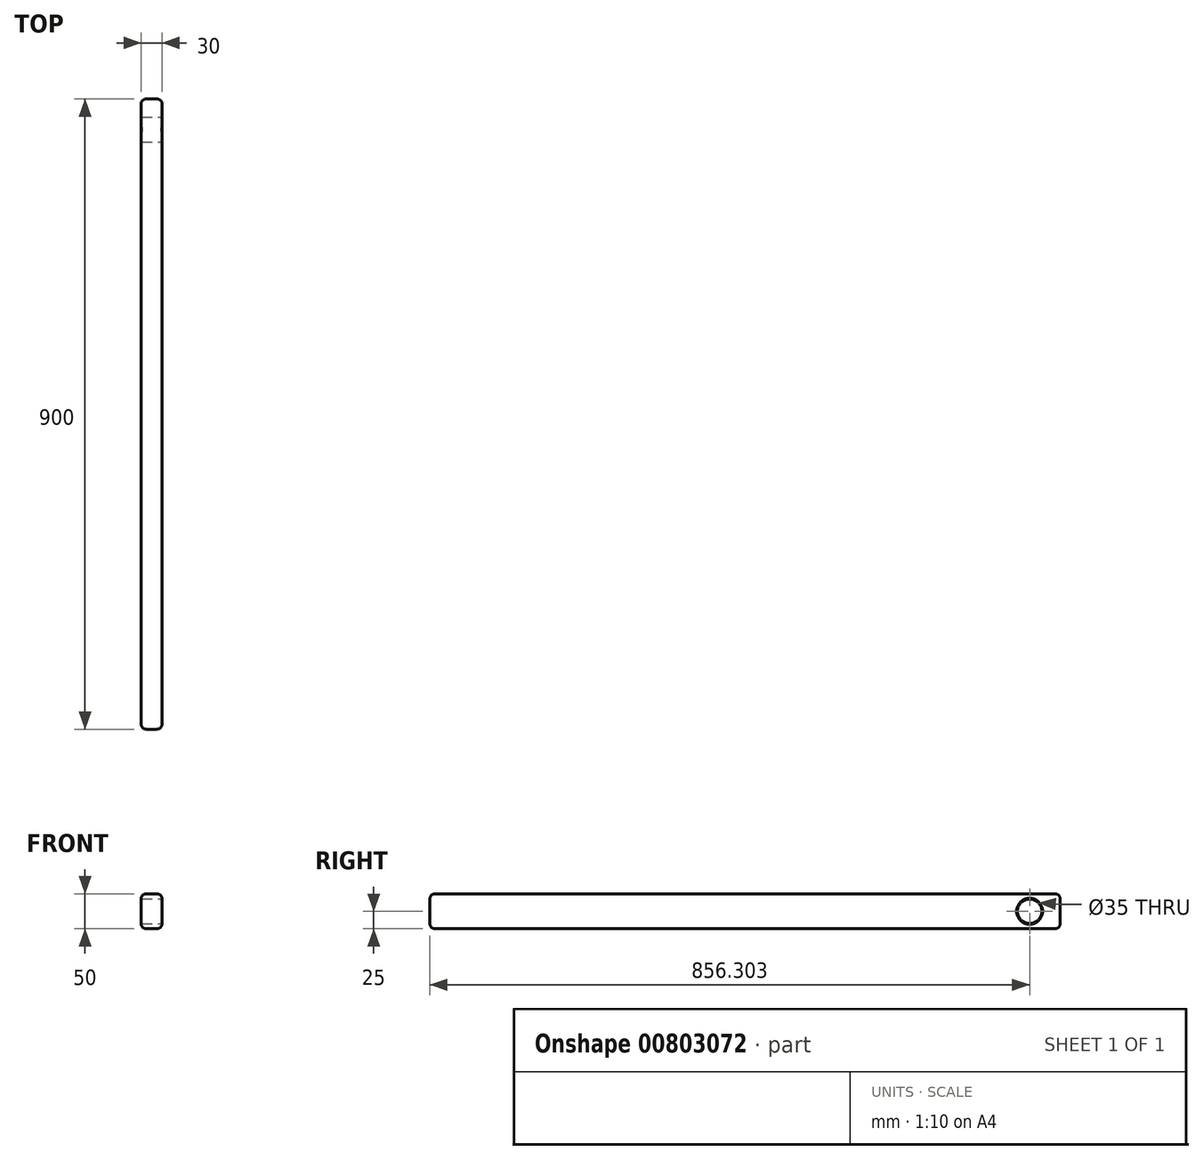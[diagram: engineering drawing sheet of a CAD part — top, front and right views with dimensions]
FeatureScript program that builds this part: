
annotation { "Feature Type Name" : "Feature", "Feature Type Description" : "" }
export const myFeature = defineFeature(function(context is Context, id is Id, definition is map)
    precondition{}
    {
        {
            var Q0;
            Q0=qCreatedBy(makeId("Front.planeOp"),FACE);
            var sketch = newSketch(context, id + "F0", { "sketchPlane" : qUnion([Q0])});
            skLineSegment(sketch, "E0.bottom", {"start": v(0, 0) * mm, "end": v(30, 0) * mm});
            skLineSegment(sketch, "E0.top", {"start": v(0, -50) * mm, "end": v(30, -50) * mm});
            skLineSegment(sketch, "E0.left", {"start": v(0, 0) * mm, "end": v(0, -50) * mm});
            skLineSegment(sketch, "E0.right", {"start": v(30, 0) * mm, "end": v(30, -50) * mm});
            skSolve(sketch);
        }
        {
            var Q0;
            Q0=makeQuery(id+"F0.imprint","IMPRINT",FACE,{"disambiguationData":[TD([[makeQuery(id+"F0.imprint","IMPRINT",EDGE,{"derivedFrom":sQuery(id+"F0.wireOp",EDGE,"E0.bottom")}),-1.0]])]});
            extrude(context, id + "F1", {"entities" : qUnion([Q0]), "depth" : 900 * mm, "offsetDistance" : 25.4 * mm});
        }
        {
            var Q0;
            Q0=makeQuery(id+"F1.opExtrude","SWEPT_EDGE",EDGE,{"disambiguationData":[OSD([sQuery(id+"F0.wireOp",EDGE,"E0.bottom"),sQuery(id+"F0.wireOp",EDGE,"E0.left")])]});
            var Q1;
            Q1=makeQuery(id+"F1.opExtrude","SWEPT_EDGE",EDGE,{"disambiguationData":[OSD([sQuery(id+"F0.wireOp",EDGE,"E0.bottom"),sQuery(id+"F0.wireOp",EDGE,"E0.right")])]});
            var Q2;
            Q2=makeQuery(id+"F1.opExtrude","CAP_EDGE",EDGE,{"disambiguationData":[OSD([sQuery(id+"F0.wireOp",EDGE,"E0.bottom")])],"isStart":true});
            var Q3;
            Q3=makeQuery(id+"F1.opExtrude","CAP_EDGE",EDGE,{"disambiguationData":[OSD([sQuery(id+"F0.wireOp",EDGE,"E0.left")])],"isStart":true});
            var Q4;
            Q4=makeQuery(id+"F1.opExtrude","CAP_EDGE",EDGE,{"disambiguationData":[OSD([sQuery(id+"F0.wireOp",EDGE,"E0.top")])],"isStart":true});
            var Q5;
            Q5=makeQuery(id+"F1.opExtrude","CAP_EDGE",EDGE,{"disambiguationData":[OSD([sQuery(id+"F0.wireOp",EDGE,"E0.right")])],"isStart":true});
            var Q6;
            Q6=makeQuery(id+"F1.opExtrude","SWEPT_EDGE",EDGE,{"disambiguationData":[OSD([sQuery(id+"F0.wireOp",EDGE,"E0.top"),sQuery(id+"F0.wireOp",EDGE,"E0.right")])]});
            var Q7;
            Q7=makeQuery(id+"F1.opExtrude","SWEPT_EDGE",EDGE,{"disambiguationData":[OSD([sQuery(id+"F0.wireOp",EDGE,"E0.top"),sQuery(id+"F0.wireOp",EDGE,"E0.left")])]});
            var Q8;
            Q8=makeQuery(id+"F1.opExtrude","CAP_EDGE",EDGE,{"disambiguationData":[OSD([sQuery(id+"F0.wireOp",EDGE,"E0.top")])],"isStart":false});
            var Q9;
            Q9=makeQuery(id+"F1.opExtrude","CAP_EDGE",EDGE,{"disambiguationData":[OSD([sQuery(id+"F0.wireOp",EDGE,"E0.left")])],"isStart":false});
            var Q10;
            Q10=makeQuery(id+"F1.opExtrude","CAP_EDGE",EDGE,{"disambiguationData":[OSD([sQuery(id+"F0.wireOp",EDGE,"E0.bottom")])],"isStart":false});
            var Q11;
            Q11=makeQuery(id+"F1.opExtrude","CAP_EDGE",EDGE,{"disambiguationData":[OSD([sQuery(id+"F0.wireOp",EDGE,"E0.right")])],"isStart":false});
            fillet(context, id + "F2", {"entities" : qUnion([Q0, Q1, Q2, Q3, Q4, Q5, Q6, Q7, Q8, Q9, Q10, Q11]), "radius" : 7.5 * mm, "tangentPropagation" : true, "allowEdgeOverflow" : false});
        }
        {
            var Q0;
            Q0=makeQuery(id+"F1.opExtrude","SWEPT_FACE",FACE,{"disambiguationData":[OSD([sQuery(id+"F0.wireOp",EDGE,"E0.right")])]});
            var sketch = newSketch(context, id + "F3", { "sketchPlane" : qUnion([Q0])});
            skCircle(sketch, "E1", {"center": v(-43.7, -25) * mm, "radius": 17.5 * mm});
            skPoint(sketch, "E1.centerSnap0", {"position": v(-7.5, -25) * mm});
            skSolve(sketch);
        }
        {
            var Q0;
            {var subQ0=sQuery(id+"F3.wireOp",EDGE,"E1");var subQ1=sQuery(id+"F0.wireOp",EDGE,"E0.right");var subQ2=makeQuery(id+"F1.opExtrude","SWEPT_FACE",FACE,{"disambiguationData":[OSD([subQ1])]});var subQ3=makeQuery(id+"F3.imprint","INTERSECT",VERTEX,{"derivedFrom":[makeQuery(id+"F2.opFillet","BLEND_EDGE",EDGE,{"blendedFrom":[makeQuery(id+"F1.opExtrude","SWEPT_EDGE",EDGE,{"disambiguationData":[OSD([sQuery(id+"F0.wireOp",EDGE,"E0.bottom"),subQ1])]}),subQ2],"blendedInto":[subQ2]}),subQ0]});Q0=makeQuery(id+"F3.imprint","IMPRINT",FACE,{"disambiguationData":[TD([[makeQuery(id+"F3.imprint","IMPRINT",EDGE,{"disambiguationData":[TD([[subQ3,-1.0]])],"derivedFrom":subQ0}),1.0]])]});}
            var Q1;
            Q1=sQuery(id+"F3.wireOp",EDGE,"E1");
            extrude(context, id + "F4", {"entities" : qUnion([Q0]), "operationType" : NewBodyOperationType.REMOVE, "surfaceEntities" : qUnion([Q1]), "oppositeDirection" : true, "depth" : 50 * mm, "offsetDistance" : 25.4 * mm});
        }
        {
            var Q0;
            Q0=makeQuery(id+"F4.boolean.opBoolean","INTERSECT",EDGE,{"disambiguationData":[OD(1.0)],"derivedFrom":[makeQuery(id+"F1.opExtrude","SWEPT_FACE",FACE,{"disambiguationData":[OSD([sQuery(id+"F0.wireOp",EDGE,"E0.left")])]}),makeQuery(id+"F4.opExtrude","SWEPT_FACE",FACE,{"disambiguationData":[OSD([sQuery(id+"F3.wireOp",EDGE,"E1")])]})]});
            var Q1;
            Q1=makeQuery(id+"F4.boolean.opBoolean","INTERSECT",EDGE,{"disambiguationData":[OD(0.0)],"derivedFrom":[makeQuery(id+"F1.opExtrude","SWEPT_FACE",FACE,{"disambiguationData":[OSD([sQuery(id+"F0.wireOp",EDGE,"E0.left")])]}),makeQuery(id+"F4.opExtrude","SWEPT_FACE",FACE,{"disambiguationData":[OSD([sQuery(id+"F3.wireOp",EDGE,"E1")])]})]});
            var Q2;
            Q2=makeQuery(id+"F4.boolean.opBoolean","COPY",EDGE,{"disambiguationData":[OD(0.0)],"derivedFrom":makeQuery(id+"F4.opExtrude","CAP_EDGE",EDGE,{"disambiguationData":[OSD([sQuery(id+"F3.wireOp",EDGE,"E1")])],"isStart":true})});
            var Q3;
            Q3=makeQuery(id+"F4.boolean.opBoolean","COPY",FACE,{"derivedFrom":makeQuery(id+"F4.opExtrude","SWEPT_FACE",FACE,{"disambiguationData":[OSD([sQuery(id+"F3.wireOp",EDGE,"E1")])]})});
            var Q4;
            Q4=makeQuery(id+"F4.boolean.opBoolean","COPY",EDGE,{"disambiguationData":[OD(1.0)],"derivedFrom":makeQuery(id+"F4.opExtrude","CAP_EDGE",EDGE,{"disambiguationData":[OSD([sQuery(id+"F3.wireOp",EDGE,"E1")])],"isStart":true})});
            chamfer(context, id + "F5", {"entities" : qUnion([Q0, Q1, Q2, Q3, Q4]), "width" : 1 * mm, "tangentPropagation" : true});
        }
    });
